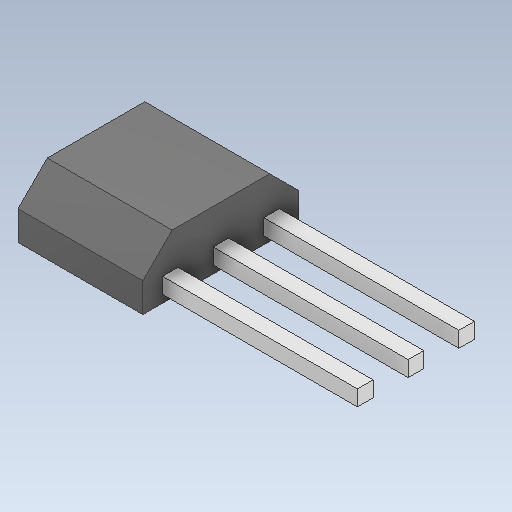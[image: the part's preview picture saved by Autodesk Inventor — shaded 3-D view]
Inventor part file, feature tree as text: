
AUTODESK INVENTOR PART (.ipt)
format: ipt  version: 2020 (Build 240168000, 168)  size: 140,288 bytes
history: native  units: mm
features: extrude x2, sketch x2
ambient origin geometry x8: Origin, YZ Plane, XZ Plane, XY Plane, X Axis, Y Axis, Z Axis, Center Point
bodies: Volumenkörper1 (feature_tree)
feature tree (4):
  extrude  "Extrusion1"  Depth=1.5mm
  extrude  "Extrusion2"  TaperAngle=45.0deg  [1 undecoded]
  sketch  "Skizze1"  dims[d0=4.0mm d1=1.5mm]
  sketch  "Skizze2"  dims[d2=0.75mm d3=45.0deg d4=3.2mm d5=0.0mm d6=0.4mm d7=3.0mm d8=0.9mm d9=5.0mm d10=0.0mm]
note: 1 required parameter value undecoded (feature->parameter linkage not recoverable at this tier; creation-order binding heuristic only, values carry confidence <= 0.55)
